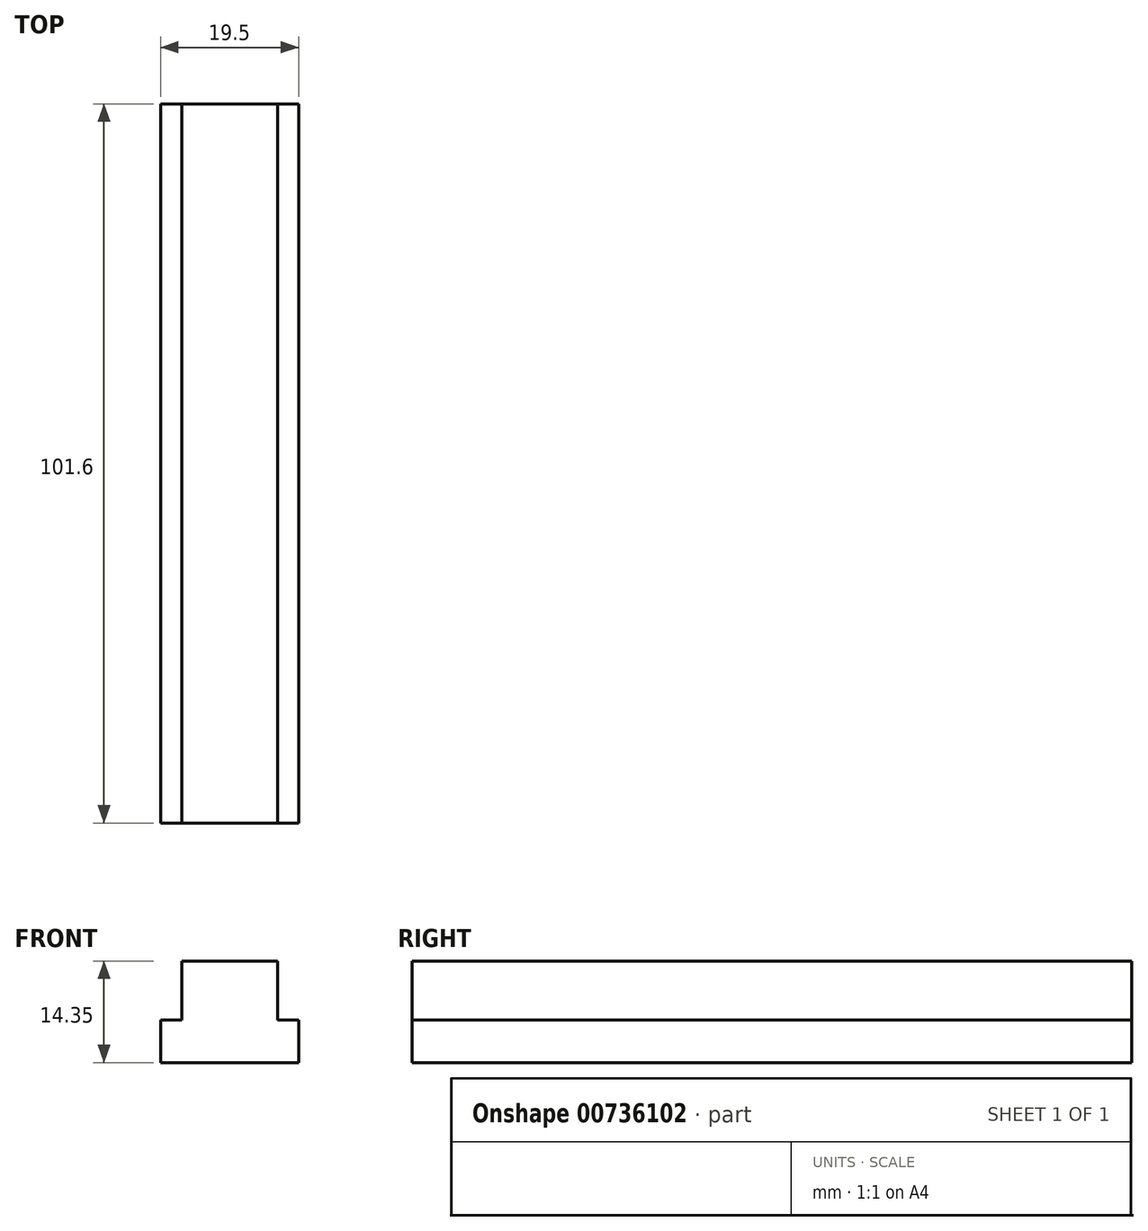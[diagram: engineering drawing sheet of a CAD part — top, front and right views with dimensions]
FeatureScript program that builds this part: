
annotation { "Feature Type Name" : "Feature", "Feature Type Description" : "" }
export const myFeature = defineFeature(function(context is Context, id is Id, definition is map)
    precondition{}
    {
        {
            var Q0;
            Q0=qCreatedBy(makeId("Front.planeOp"),FACE);
            var sketch = newSketch(context, id + "F0", { "sketchPlane" : qUnion([Q0])});
            skLineSegment(sketch, "E0.bottom", {"start": v(0, 0) * mm, "end": v(19.5, 0) * mm});
            skLineSegment(sketch, "E0.left", {"start": v(0, 0) * mm, "end": v(0, 6) * mm});
            skLineSegment(sketch, "E0.right", {"start": v(19.5, 0) * mm, "end": v(19.5, 6) * mm});
            skLineSegment(sketch, "E1.bottom", {"start": v(3, 1.62) * mm, "end": v(16.5, 1.62) * mm});
            skLineSegment(sketch, "E1.left", {"start": v(3, 1.62) * mm, "end": v(3, 14.35) * mm});
            skLineSegment(sketch, "E1.right", {"start": v(16.5, 1.62) * mm, "end": v(16.5, 14.35) * mm});
            skLineSegment(sketch, "E2.bottom", {"start": v(3, 14.35) * mm, "end": v(16.5, 14.35) * mm});
            skLineSegment(sketch, "E2.top", {"start": v(3, 14.35) * mm, "end": v(16.5, 14.35) * mm});
            skLineSegment(sketch, "E2.left", {"start": v(3, 14.35) * mm, "end": v(3, 14.35) * mm});
            skLineSegment(sketch, "E2.right", {"start": v(16.5, 14.35) * mm, "end": v(16.5, 14.35) * mm});
            skPoint(sketch, "E3", {"position": v(3, 6) * mm});
            skPoint(sketch, "E4", {"position": v(16.5, 6) * mm});
            skLineSegment(sketch, "E5", {"start": v(0, 6) * mm, "end": v(3, 6) * mm});
            skLineSegment(sketch, "E6", {"start": v(16.5, 6) * mm, "end": v(19.5, 6) * mm});
            skSolve(sketch);
        }
        {
            var Q0;
            Q0=makeQuery(id+"F0.imprint","IMPRINT",FACE,{"disambiguationData":[TD([[makeQuery(id+"F0.imprint","IMPRINT",EDGE,{"derivedFrom":sQuery(id+"F0.wireOp",EDGE,"E0.bottom")}),1.0]])]});
            var Q1;
            {var subQ1=sQuery(id+"F0.wireOp",EDGE,"E1.bottom");Q1=makeQuery(id+"F0.imprint","IMPRINT",FACE,{"disambiguationData":[TD([[makeQuery(id+"F0.imprint","IMPRINT",EDGE,{"derivedFrom":subQ1}),1.0]])]});}
            extrude(context, id + "F1", {"entities" : qUnion([Q0, Q1]), "depth" : 101.6 * mm, "offsetDistance" : 25.4 * mm});
        }
    });
